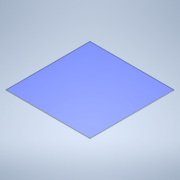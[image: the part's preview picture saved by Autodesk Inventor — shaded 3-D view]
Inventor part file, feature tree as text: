
AUTODESK INVENTOR PART (.ipt)
format: ipt  version: 2020 (Build 240168000, 168)  size: 97,792 bytes
history: native  units: in
note: dims shown in document units (in); Inventor stores cm internally (conversion verified against a paired STEP export)
features: extrude x1, sketch x1
ambient origin geometry x8: Origin, YZ Plane, XZ Plane, XY Plane, X Axis, Y Axis, Z Axis, Center Point
bodies: Solid1 (feature_tree)
feature tree (2):
  extrude  "Extrusion1"  Depth=1.0in
  sketch  "Sketch1"  dims[d0=1.0in d1=1.0in d2=0.0067in d3=0.0in]
